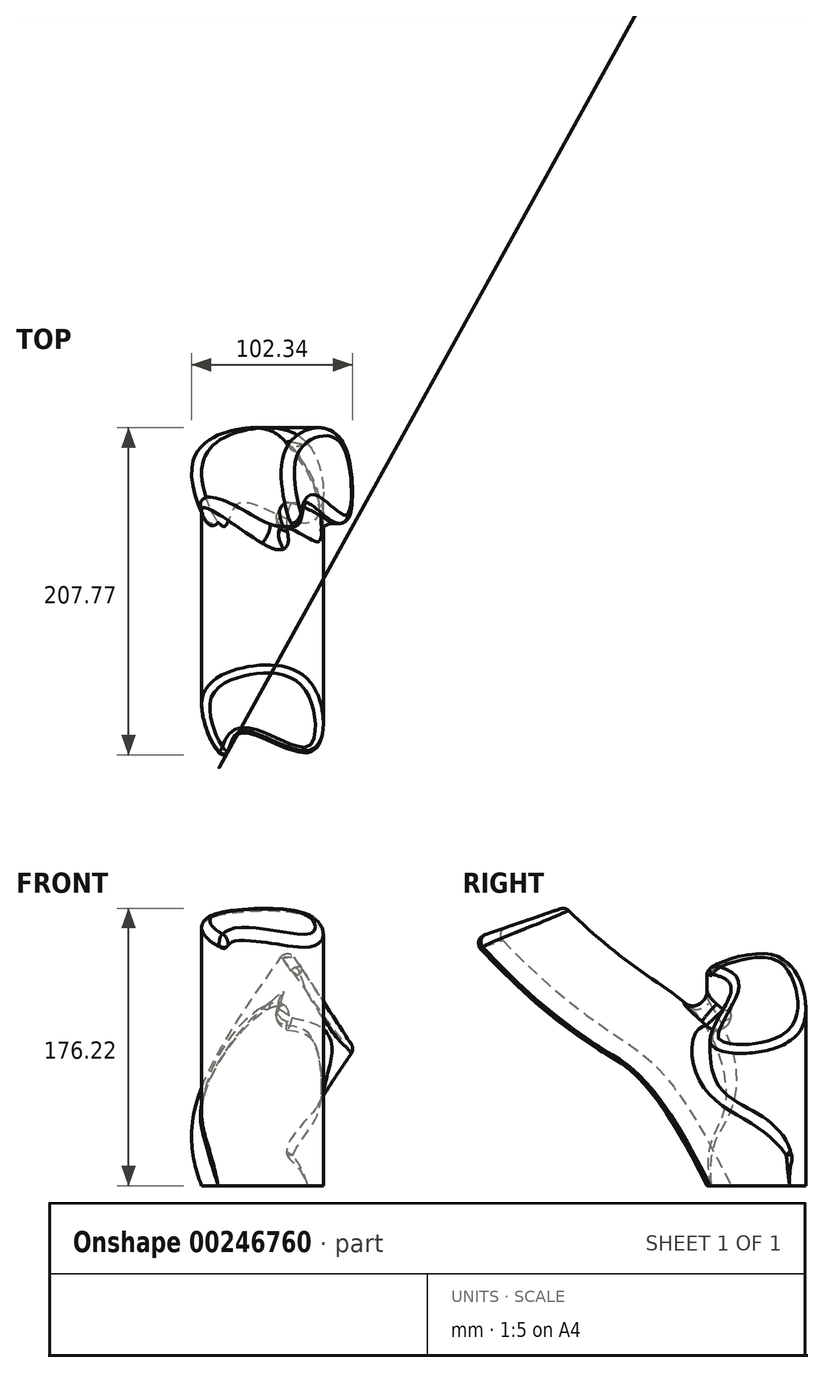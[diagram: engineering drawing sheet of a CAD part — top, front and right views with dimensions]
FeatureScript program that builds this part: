
annotation { "Feature Type Name" : "Feature", "Feature Type Description" : "" }
export const myFeature = defineFeature(function(context is Context, id is Id, definition is map)
    precondition{}
    {
        {
            var Q0;
            Q0=qCreatedBy(makeId("Top.planeOp"),FACE);
            var sketch = newSketch(context, id + "F0", { "sketchPlane" : qUnion([Q0])});
            skFitSpline(sketch, "E0", {"points": [v(-15.7, -43.72) * mm, v(-29.97, -6.41) * mm, v(0, 17.84) * mm, v(40.05, 4.97) * mm, v(38.73, -41.35) * mm, v(-6.32, -29.07) * mm, v(-15.7, -43.72) * mm]});
            skSolve(sketch);
        }
        {
            var Q0;
            Q0=qCreatedBy(makeId("Front.planeOp"),FACE);
            var sketch = newSketch(context, id + "F1", { "sketchPlane" : qUnion([Q0])});
            skFitSpline(sketch, "E1", {"points": [v(0, 0) * mm, v(-7.15, 38.72) * mm, v(41.09, 126.27) * mm], "startDerivative": vector(-37.24, 92.3) * mm, "endDerivative": vector(108.32, 155.43) * mm});
            skSolve(sketch);
        }
        {
            var Q0;
            Q0=makeQuery(id+"F0.imprint","IMPRINT",FACE,{"disambiguationData":[TD([[makeQuery(id+"F0.imprint","IMPRINT",EDGE,{"derivedFrom":sQuery(id+"F0.wireOp",EDGE,"E0")}),-1.0]])]});
            var Q1;
            Q1=sQuery(id+"F0.wireOp",EDGE,"E0");
            var Q2;
            Q2=sQuery(id+"F1.wireOp",EDGE,"E1");
            sweep(context, id + "F2", {"profiles" : qUnion([Q0]), "surfaceProfiles" : qUnion([Q1]), "path" : qUnion([Q2])});
        }
        {
            var Q0;
            Q0=qCreatedBy(makeId("Right.planeOp"),FACE);
            var sketch = newSketch(context, id + "F3", { "sketchPlane" : qUnion([Q0])});
            skFitSpline(sketch, "E2", {"points": [v(0, 0) * mm, v(-60.74, 95.87) * mm, v(-151.85, 170.82) * mm], "startDerivative": vector(-126.46, 267.85) * mm, "endDerivative": vector(-258.42, 265.62) * mm});
            skSolve(sketch);
        }
        {
            var Q0;
            Q0=makeQuery(id+"F0.imprint","IMPRINT",FACE,{"disambiguationData":[TD([[makeQuery(id+"F0.imprint","IMPRINT",EDGE,{"derivedFrom":sQuery(id+"F0.wireOp",EDGE,"E0")}),-1.0]])]});
            var Q1;
            Q1=makeQuery(id+"F2.opSweep","CAP_EDGE",EDGE,{"disambiguationData":[OSD([sQuery(id+"F0.wireOp",EDGE,"E0"),sQuery(id+"F1.wireOp",VERTEX,"E1.start")])],"isStart":true});
            var Q2;
            Q2=sQuery(id+"F3.wireOp",EDGE,"E2");
            sweep(context, id + "F4", {"profiles" : qUnion([Q0]), "surfaceProfiles" : qUnion([Q1]), "path" : qUnion([Q2])});
        }
        {
            var Q0;
            Q0=makeQuery(id+"F4.opSweep","SWEPT_BODY",BODY,{"disambiguationData":[OSD([sQuery(id+"F0.wireOp",EDGE,"E0"),sQuery(id+"F3.wireOp",EDGE,"E2")])]});
            var Q1;
            Q1=makeQuery(id+"F2.opSweep","SWEPT_BODY",BODY,{"disambiguationData":[OSD([sQuery(id+"F0.wireOp",EDGE,"E0"),sQuery(id+"F1.wireOp",EDGE,"E1")])]});
            booleanBodies(context, id + "F5", {"operationType" : BooleanOperationType.UNION, "tools" : qUnion([Q0, Q1])});
        }
        {
            var Q0;
            {var subQ0=sQuery(id+"F0.wireOp",EDGE,"E0");Q0=makeQuery(id+"F5.opBoolean","INTERSECT",EDGE,{"derivedFrom":[makeQuery(id+"F2.opSweep","SWEPT_FACE",FACE,{"disambiguationData":[OSD([subQ0,sQuery(id+"F1.wireOp",EDGE,"E1")])]}),makeQuery(id+"F4.opSweep","SWEPT_FACE",FACE,{"disambiguationData":[OSD([subQ0,sQuery(id+"F3.wireOp",EDGE,"E2")])]})]});}
            fillet(context, id + "F6", {"entities" : qUnion([Q0]), "radius" : 9.17 * mm, "tangentPropagation" : true, "allowEdgeOverflow" : false});
        }
        {
            var Q0;
            Q0=makeQuery(id+"F4.opSweep","CAP_EDGE",EDGE,{"disambiguationData":[OSD([sQuery(id+"F0.wireOp",EDGE,"E0"),sQuery(id+"F3.wireOp",VERTEX,"E2.end")])],"isStart":false});
            var Q1;
            Q1=makeQuery(id+"F2.opSweep","CAP_EDGE",EDGE,{"disambiguationData":[OSD([sQuery(id+"F0.wireOp",EDGE,"E0"),sQuery(id+"F1.wireOp",VERTEX,"E1.end")])],"isStart":false});
            fillet(context, id + "F7", {"entities" : qUnion([Q0, Q1]), "radius" : 5.08 * mm, "tangentPropagation" : true, "allowEdgeOverflow" : false});
        }
    });
